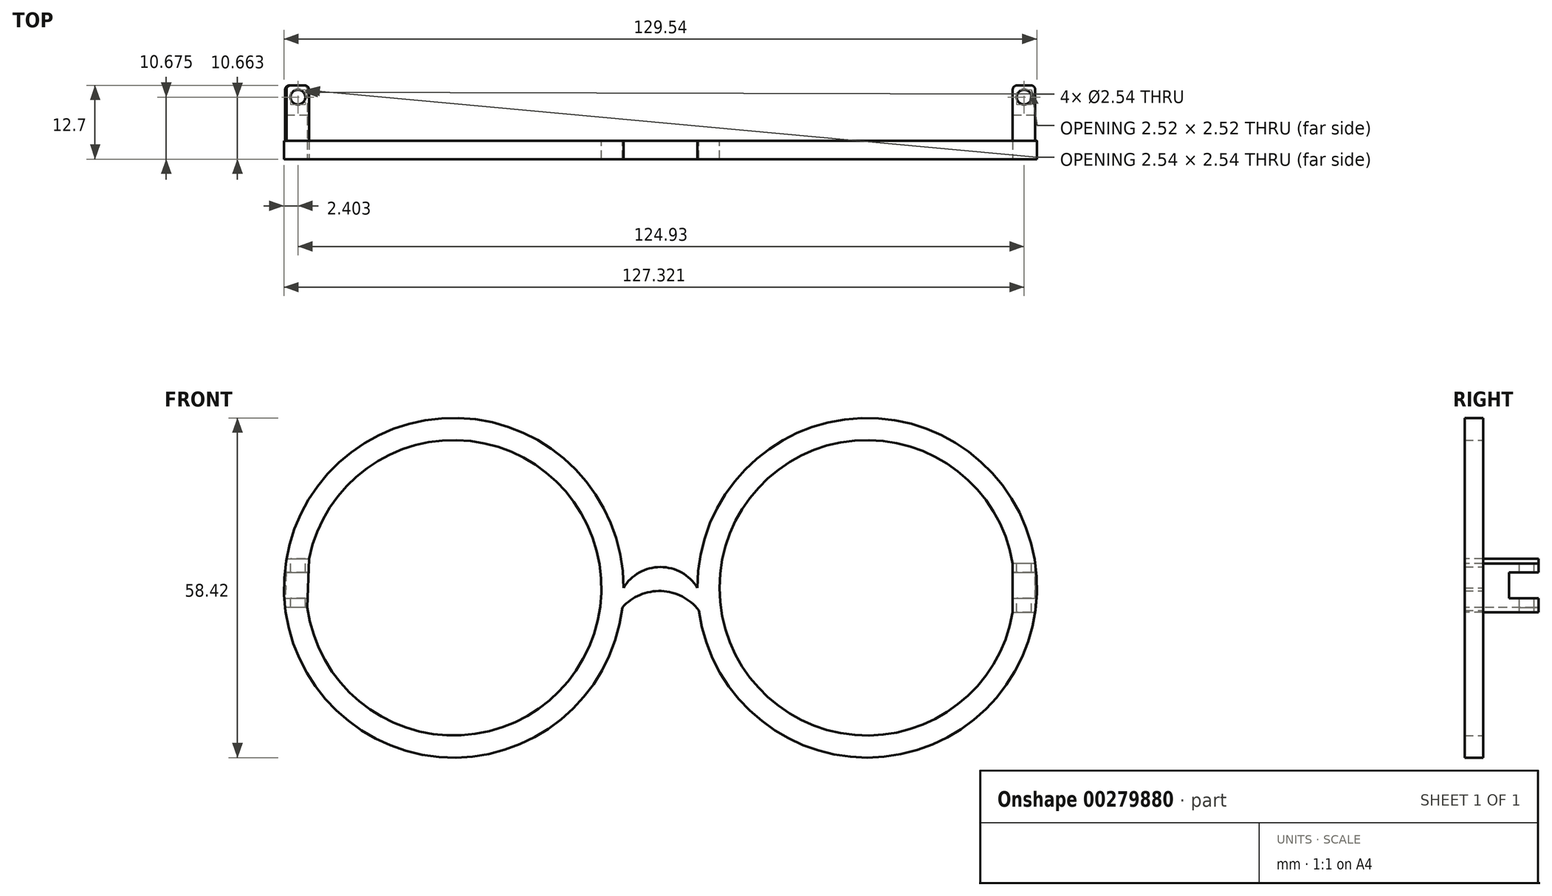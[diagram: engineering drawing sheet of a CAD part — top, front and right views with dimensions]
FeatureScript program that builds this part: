
annotation { "Feature Type Name" : "Feature", "Feature Type Description" : "" }
export const myFeature = defineFeature(function(context is Context, id is Id, definition is map)
    precondition{}
    {
        {
            var Q0;
            Q0=qCreatedBy(makeId("Front.planeOp"),FACE);
            var sketch = newSketch(context, id + "F0", { "sketchPlane" : qUnion([Q0])});
            skCircle(sketch, "E0", {"center": v(-47.12, 0) * mm, "radius": 29.21 * mm});
            skCircle(sketch, "E1", {"center": v(24, 0) * mm, "radius": 29.21 * mm});
            skArc(sketch, "E2", {"start": v(-5.2, 0) * mm, "mid": v(-11.56, 3.57) * mm, "end": v(-17.9, 0) * mm});
            skArc(sketch, "E3", {"start": v(-4.95, -3.87) * mm, "mid": v(-11.41, -0.56) * mm, "end": v(-18.1, -3.37) * mm});
            skCircle(sketch, "E4", {"center": v(-47.12, 0) * mm, "radius": 25.4 * mm});
            skCircle(sketch, "E5", {"center": v(24, 0) * mm, "radius": 25.4 * mm});
            skLineSegment(sketch, "E6", {"start": v(-76.16, -3.18) * mm, "end": v(-72.32, -3.18) * mm});
            skLineSegment(sketch, "E7", {"start": v(-76.33, 0) * mm, "end": v(-72.52, 0) * mm});
            skLineSegment(sketch, "E8", {"start": v(49.4, 0) * mm, "end": v(53.21, 0) * mm});
            skLineSegment(sketch, "E9", {"start": v(49.2, -3.18) * mm, "end": v(53.04, -3.18) * mm});
            skSolve(sketch);
        }
        {
            var Q0;
            Q0 = qSketchRegion(id + "F0", true);
            extrude(context, id + "F1", {"entities" : qUnion([Q0]), "depth" : 3.17 * mm});
        }
        {
            var Q0;
            Q0=makeQuery(id+"F1.opExtrude","CAP_FACE",FACE,{"disambiguationData":[OSD([sQuery(id+"F0.wireOp",EDGE,"E0"),sQuery(id+"F0.wireOp",EDGE,"E1"),sQuery(id+"F0.wireOp",EDGE,"E2"),sQuery(id+"F0.wireOp",EDGE,"E3"),sQuery(id+"F0.wireOp",EDGE,"E4"),sQuery(id+"F0.wireOp",EDGE,"E5")])],"isStart":false});
            var sketch = newSketch(context, id + "F2", { "sketchPlane" : qUnion([Q0])});
            skLineSegment(sketch, "E10", {"start": v(49.05, 4.2) * mm, "end": v(49.05, -4.2) * mm});
            skLineSegment(sketch, "E11", {"start": v(49.05, -4.2) * mm, "end": v(52.9, -4.2) * mm});
            skLineSegment(sketch, "E12", {"start": v(52.9, -4.2) * mm, "end": v(52.9, 4.2) * mm});
            skLineSegment(sketch, "E13", {"start": v(52.9, 4.2) * mm, "end": v(49.05, 4.2) * mm});
            skLineSegment(sketch, "E14", {"start": v(-76.13, -3.37) * mm, "end": v(-75.9, 5) * mm});
            skLineSegment(sketch, "E15", {"start": v(-75.9, 5) * mm, "end": v(-72.02, 5) * mm});
            skLineSegment(sketch, "E16", {"start": v(-72.02, 5) * mm, "end": v(-72.3, -3.37) * mm});
            skLineSegment(sketch, "E17", {"start": v(-72.3, -3.37) * mm, "end": v(-76.13, -3.37) * mm});
            skSolve(sketch);
        }
        {
            var Q0;
            Q0 = qSketchRegion(id + "F2", true);
            extrude(context, id + "F3", {"entities" : qUnion([Q0]), "operationType" : NewBodyOperationType.ADD, "oppositeDirection" : true, "depth" : 12.7 * mm});
        }
        {
            var Q0;
            Q0=makeQuery(id+"F3.opExtrude","SWEPT_FACE",FACE,{"disambiguationData":[OSD([sQuery(id+"F2.wireOp",EDGE,"E12")])]});
            var sketch = newSketch(context, id + "F4", { "sketchPlane" : qUnion([Q0])});
            skLineSegment(sketch, "E18", {"start": v(9.53, 2.64) * mm, "end": v(4.44, 2.64) * mm});
            skLineSegment(sketch, "E19", {"start": v(4.44, 2.64) * mm, "end": v(4.44, -1.8) * mm});
            skLineSegment(sketch, "E20", {"start": v(4.44, -1.8) * mm, "end": v(9.53, -1.8) * mm});
            skLineSegment(sketch, "E21", {"start": v(9.53, -1.8) * mm, "end": v(9.53, 2.64) * mm});
            skSolve(sketch);
        }
        {
            var Q0;
            Q0=makeQuery(id+"F4.imprint","IMPRINT",FACE,{"disambiguationData":[TD([[makeQuery(id+"F4.imprint","IMPRINT",EDGE,{"derivedFrom":sQuery(id+"F4.wireOp",EDGE,"E18")}),1.0]])]});
            extrude(context, id + "F5", {"entities" : qUnion([Q0]), "operationType" : NewBodyOperationType.REMOVE, "endBound" : BoundingType.THROUGH_ALL, "oppositeDirection" : true, "depth" : 25.4 * mm});
        }
        {
            var Q0;
            Q0=makeQuery(id+"F3.opExtrude","SWEPT_FACE",FACE,{"disambiguationData":[OSD([sQuery(id+"F2.wireOp",EDGE,"E13")])]});
            var sketch = newSketch(context, id + "F6", { "sketchPlane" : qUnion([Q0])});
            skCircle(sketch, "E22", {"center": v(51, 7.5) * mm, "radius": 1.27 * mm});
            skSolve(sketch);
        }
        {
            var Q0;
            Q0=makeQuery(id+"F6.imprint","IMPRINT",FACE,{"disambiguationData":[TD([[makeQuery(id+"F6.imprint","IMPRINT",EDGE,{"derivedFrom":sQuery(id+"F6.wireOp",EDGE,"E22")}),1.0]])]});
            extrude(context, id + "F7", {"entities" : qUnion([Q0]), "operationType" : NewBodyOperationType.REMOVE, "endBound" : BoundingType.THROUGH_ALL, "oppositeDirection" : true, "depth" : 25.4 * mm});
        }
        {
            var Q0;
            Q0=makeQuery(id+"F3.opExtrude","SWEPT_FACE",FACE,{"disambiguationData":[OSD([sQuery(id+"F2.wireOp",EDGE,"E15")])]});
            var sketch = newSketch(context, id + "F8", { "sketchPlane" : qUnion([Q0])});
            skCircle(sketch, "E23", {"center": v(-73.93, 7.5) * mm, "radius": 1.27 * mm});
            skSolve(sketch);
        }
        {
            var Q0;
            Q0=makeQuery(id+"F8.imprint","IMPRINT",FACE,{"disambiguationData":[TD([[makeQuery(id+"F8.imprint","IMPRINT",EDGE,{"derivedFrom":sQuery(id+"F8.wireOp",EDGE,"E23")}),1.0]])]});
            extrude(context, id + "F9", {"entities" : qUnion([Q0]), "operationType" : NewBodyOperationType.REMOVE, "endBound" : BoundingType.THROUGH_ALL, "oppositeDirection" : true, "depth" : 25.4 * mm});
        }
        {
            var Q0;
            {var subQ0=sQuery(id+"F2.wireOp",EDGE,"E10");var subQ1=sQuery(id+"F2.wireOp",EDGE,"E13");Q0=makeQuery(id+"F5.boolean.opBoolean","SPLIT",EDGE,{"disambiguationData":[TD([makeQuery(id+"F3.opExtrude","SWEPT_FACE",FACE,{"disambiguationData":[OSD([subQ1])]})])],"derivedFrom":makeQuery(id+"F3.opExtrude","CAP_EDGE",EDGE,{"disambiguationData":[OSD([subQ0])],"isStart":false})});}
            var Q1;
            {var subQ0=sQuery(id+"F2.wireOp",EDGE,"E13");var subQ1=sQuery(id+"F2.wireOp",EDGE,"E12");Q1=makeQuery(id+"F5.boolean.opBoolean","SPLIT",EDGE,{"disambiguationData":[TD([makeQuery(id+"F3.opExtrude","SWEPT_FACE",FACE,{"disambiguationData":[OSD([subQ0])]})])],"derivedFrom":makeQuery(id+"F3.opExtrude","CAP_EDGE",EDGE,{"disambiguationData":[OSD([subQ1])],"isStart":false})});}
            var Q2;
            {var subQ0=sQuery(id+"F2.wireOp",EDGE,"E12");var subQ1=sQuery(id+"F2.wireOp",EDGE,"E11");Q2=makeQuery(id+"F5.boolean.opBoolean","SPLIT",EDGE,{"disambiguationData":[TD([makeQuery(id+"F3.opExtrude","SWEPT_FACE",FACE,{"disambiguationData":[OSD([subQ1])]})])],"derivedFrom":makeQuery(id+"F3.opExtrude","CAP_EDGE",EDGE,{"disambiguationData":[OSD([subQ0])],"isStart":false})});}
            var Q3;
            {var subQ0=sQuery(id+"F2.wireOp",EDGE,"E10");var subQ1=sQuery(id+"F2.wireOp",EDGE,"E11");Q3=makeQuery(id+"F5.boolean.opBoolean","SPLIT",EDGE,{"disambiguationData":[TD([makeQuery(id+"F3.opExtrude","SWEPT_FACE",FACE,{"disambiguationData":[OSD([subQ1])]})])],"derivedFrom":makeQuery(id+"F3.opExtrude","CAP_EDGE",EDGE,{"disambiguationData":[OSD([subQ0])],"isStart":false})});}
            fillet(context, id + "F10", {"entities" : qUnion([Q0, Q1, Q2, Q3]), "radius" : 0.76 * mm, "tangentPropagation" : true, "allowEdgeOverflow" : false});
        }
        {
            var Q0;
            {var subQ0=sQuery(id+"F2.wireOp",EDGE,"E14");var subQ1=sQuery(id+"F2.wireOp",EDGE,"E17");Q0=makeQuery(id+"F5.boolean.opBoolean","SPLIT",EDGE,{"disambiguationData":[TD([makeQuery(id+"F3.opExtrude","SWEPT_FACE",FACE,{"disambiguationData":[OSD([subQ1])]})])],"derivedFrom":makeQuery(id+"F3.opExtrude","CAP_EDGE",EDGE,{"disambiguationData":[OSD([subQ0])],"isStart":false})});}
            var Q1;
            {var subQ0=sQuery(id+"F2.wireOp",EDGE,"E14");var subQ1=sQuery(id+"F2.wireOp",EDGE,"E15");Q1=makeQuery(id+"F5.boolean.opBoolean","SPLIT",EDGE,{"disambiguationData":[TD([makeQuery(id+"F3.opExtrude","SWEPT_FACE",FACE,{"disambiguationData":[OSD([subQ1])]})])],"derivedFrom":makeQuery(id+"F3.opExtrude","CAP_EDGE",EDGE,{"disambiguationData":[OSD([subQ0])],"isStart":false})});}
            var Q2;
            {var subQ0=sQuery(id+"F2.wireOp",EDGE,"E16");var subQ1=sQuery(id+"F2.wireOp",EDGE,"E15");Q2=makeQuery(id+"F5.boolean.opBoolean","SPLIT",EDGE,{"disambiguationData":[TD([makeQuery(id+"F3.opExtrude","SWEPT_FACE",FACE,{"disambiguationData":[OSD([subQ1])]})])],"derivedFrom":makeQuery(id+"F3.opExtrude","CAP_EDGE",EDGE,{"disambiguationData":[OSD([subQ0])],"isStart":false})});}
            var Q3;
            {var subQ0=sQuery(id+"F2.wireOp",EDGE,"E17");var subQ1=sQuery(id+"F2.wireOp",EDGE,"E16");Q3=makeQuery(id+"F5.boolean.opBoolean","SPLIT",EDGE,{"disambiguationData":[TD([makeQuery(id+"F3.opExtrude","SWEPT_FACE",FACE,{"disambiguationData":[OSD([subQ0])]})])],"derivedFrom":makeQuery(id+"F3.opExtrude","CAP_EDGE",EDGE,{"disambiguationData":[OSD([subQ1])],"isStart":false})});}
            fillet(context, id + "F11", {"entities" : qUnion([Q0, Q1, Q2, Q3]), "radius" : 0.76 * mm, "tangentPropagation" : true, "allowEdgeOverflow" : false});
        }
    });
